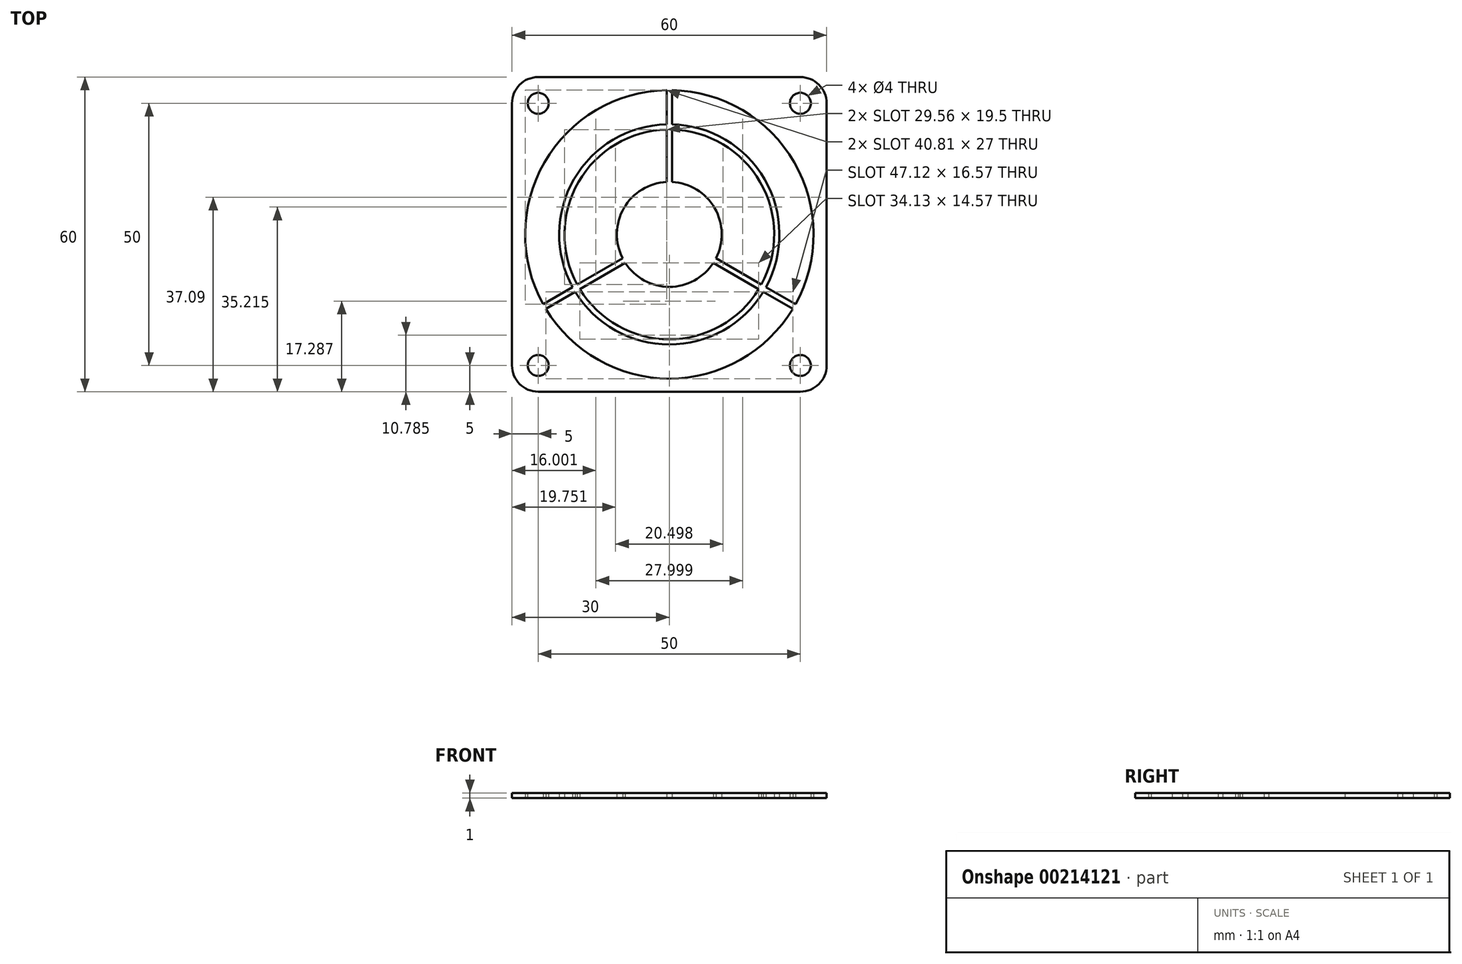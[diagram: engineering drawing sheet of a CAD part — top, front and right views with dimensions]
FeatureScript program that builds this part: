
annotation { "Feature Type Name" : "Feature", "Feature Type Description" : "" }
export const myFeature = defineFeature(function(context is Context, id is Id, definition is map)
    precondition{}
    {
        {
            var Q0;
            Q0=qCreatedBy(makeId("Top.planeOp"),FACE);
            var sketch = newSketch(context, id + "F0", { "sketchPlane" : qUnion([Q0])});
            skLineSegment(sketch, "E0.bottom", {"start": v(25, -25) * mm, "end": v(-25, -25) * mm, "construction": true});
            skLineSegment(sketch, "E0.top", {"start": v(25, 25) * mm, "end": v(-25, 25) * mm, "construction": true});
            skLineSegment(sketch, "E0.left", {"start": v(25, -25) * mm, "end": v(25, 25) * mm, "construction": true});
            skLineSegment(sketch, "E0.right", {"start": v(-25, -25) * mm, "end": v(-25, 25) * mm, "construction": true});
            skPoint(sketch, "E0.middle", {"position": v(0, 0) * mm});
            skCircle(sketch, "E1", {"center": v(-25, 25) * mm, "radius": 2 * mm});
            skCircle(sketch, "E2", {"center": v(25, 25) * mm, "radius": 2 * mm});
            skCircle(sketch, "E3", {"center": v(25, -25) * mm, "radius": 2 * mm});
            skCircle(sketch, "E4", {"center": v(-25, -25) * mm, "radius": 2 * mm});
            skArc(sketch, "E5", {"start": v(-0.5, 27.5) * mm, "mid": v(-23.82, 13.75) * mm, "end": v(-24.06, -13.31) * mm});
            skLineSegment(sketch, "E6.bottom", {"start": v(30, -30) * mm, "end": v(-30, -30) * mm});
            skLineSegment(sketch, "E6.top", {"start": v(30, 30) * mm, "end": v(-30, 30) * mm});
            skLineSegment(sketch, "E6.left", {"start": v(30, -30) * mm, "end": v(30, 30) * mm});
            skLineSegment(sketch, "E6.right", {"start": v(-30, -30) * mm, "end": v(-30, 30) * mm});
            skArc(sketch, "E7", {"start": v(-0.5, 9.99) * mm, "mid": v(-8.66, 5) * mm, "end": v(-8.9, -4.56) * mm});
            skArc(sketch, "E8", {"start": v(-17.07, -10.43) * mm, "mid": v(0, -20) * mm, "end": v(17.07, -10.43) * mm});
            skArc(sketch, "E9", {"start": v(-17.93, -10.93) * mm, "mid": v(0, -21) * mm, "end": v(17.93, -10.93) * mm});
            skLineSegment(sketch, "E10", {"start": v(0, 0) * mm, "end": v(0, 27.5) * mm, "construction": true});
            skPoint(sketch, "E10.endSnap0", {"position": v(0, 25) * mm});
            skLineSegment(sketch, "E11", {"start": v(0, 0) * mm, "end": v(-23.82, -13.75) * mm, "construction": true});
            skLineSegment(sketch, "E12", {"start": v(0, 0) * mm, "end": v(23.82, -13.75) * mm, "construction": true});
            skLineSegment(sketch, "E13.0", {"start": v(8.4, -5.43) * mm, "end": v(17.07, -10.43) * mm});
            skLineSegment(sketch, "E14.0", {"start": v(8.9, -4.56) * mm, "end": v(17.57, -9.56) * mm});
            skLineSegment(sketch, "E15.0", {"start": v(0.5, 9.99) * mm, "end": v(0.5, 20) * mm});
            skLineSegment(sketch, "E16.0", {"start": v(-0.5, 9.99) * mm, "end": v(-0.5, 20) * mm});
            skLineSegment(sketch, "E17.0", {"start": v(-8.9, -4.56) * mm, "end": v(-17.57, -9.56) * mm});
            skLineSegment(sketch, "E18.0", {"start": v(-8.4, -5.43) * mm, "end": v(-17.07, -10.43) * mm});
            skArc(sketch, "E19.trimOffspring", {"start": v(8.9, -4.56) * mm, "mid": v(8.66, 5) * mm, "end": v(0.5, 9.99) * mm});
            skArc(sketch, "E20.trimOffspring", {"start": v(-8.4, -5.43) * mm, "mid": v(0, -10) * mm, "end": v(8.4, -5.43) * mm});
            skLineSegment(sketch, "E21.trimOffspring", {"start": v(-17.93, -10.93) * mm, "end": v(-24.65, -14.8) * mm});
            skLineSegment(sketch, "E22.trimOffspring", {"start": v(-18.43, -10.06) * mm, "end": v(-24.06, -13.31) * mm});
            skLineSegment(sketch, "E23.trimOffspring", {"start": v(17.93, -10.93) * mm, "end": v(23.56, -14.18) * mm});
            skLineSegment(sketch, "E24.trimOffspring", {"start": v(18.43, -10.06) * mm, "end": v(24.06, -13.31) * mm});
            skArc(sketch, "E25.trimOffspring", {"start": v(17.57, -9.56) * mm, "mid": v(17.32, 10) * mm, "end": v(0.5, 20) * mm});
            skArc(sketch, "E26.trimOffspring", {"start": v(18.43, -10.06) * mm, "mid": v(18.19, 10.5) * mm, "end": v(0.5, 21) * mm});
            skArc(sketch, "E27.trimOffspring", {"start": v(-0.5, 20) * mm, "mid": v(-17.32, 10) * mm, "end": v(-17.57, -9.56) * mm});
            skLineSegment(sketch, "E28.trimOffspring", {"start": v(0.5, 21) * mm, "end": v(0.5, 28.75) * mm});
            skArc(sketch, "E29.trimOffspring", {"start": v(-0.5, 21) * mm, "mid": v(-18.19, 10.5) * mm, "end": v(-18.43, -10.06) * mm});
            skLineSegment(sketch, "E30.trimOffspring", {"start": v(-0.5, 21) * mm, "end": v(-0.5, 27.5) * mm});
            skArc(sketch, "E31.trimOffspring", {"start": v(-23.56, -14.18) * mm, "mid": v(0, -27.5) * mm, "end": v(23.56, -14.18) * mm});
            skArc(sketch, "E32.trimOffspring", {"start": v(24.06, -13.31) * mm, "mid": v(23.82, 13.75) * mm, "end": v(0.5, 27.5) * mm});
            skSolve(sketch);
        }
        {
            var Q0;
            Q0 = qSketchRegion(id + "F0", true);
            extrude(context, id + "F1", {"entities" : qUnion([Q0]), "depth" : 1 * mm});
        }
        {
            var Q0;
            Q0=makeQuery(id+"F1.opExtrude","SWEPT_EDGE",EDGE,{"disambiguationData":[OSD([sQuery(id+"F0.wireOp",EDGE,"E6.bottom"),sQuery(id+"F0.wireOp",EDGE,"E6.right")])]});
            var Q1;
            Q1=makeQuery(id+"F1.opExtrude","SWEPT_EDGE",EDGE,{"disambiguationData":[OSD([sQuery(id+"F0.wireOp",EDGE,"E6.bottom"),sQuery(id+"F0.wireOp",EDGE,"E6.left")])]});
            var Q2;
            Q2=makeQuery(id+"F1.opExtrude","SWEPT_EDGE",EDGE,{"disambiguationData":[OSD([sQuery(id+"F0.wireOp",EDGE,"E6.top"),sQuery(id+"F0.wireOp",EDGE,"E6.right")])]});
            var Q3;
            Q3=makeQuery(id+"F1.opExtrude","SWEPT_EDGE",EDGE,{"disambiguationData":[OSD([sQuery(id+"F0.wireOp",EDGE,"E6.top"),sQuery(id+"F0.wireOp",EDGE,"E6.left")])]});
            fillet(context, id + "F2", {"entities" : qUnion([Q0, Q1, Q2, Q3]), "radius" : 5 * mm, "tangentPropagation" : true, "allowEdgeOverflow" : false});
        }
    });
